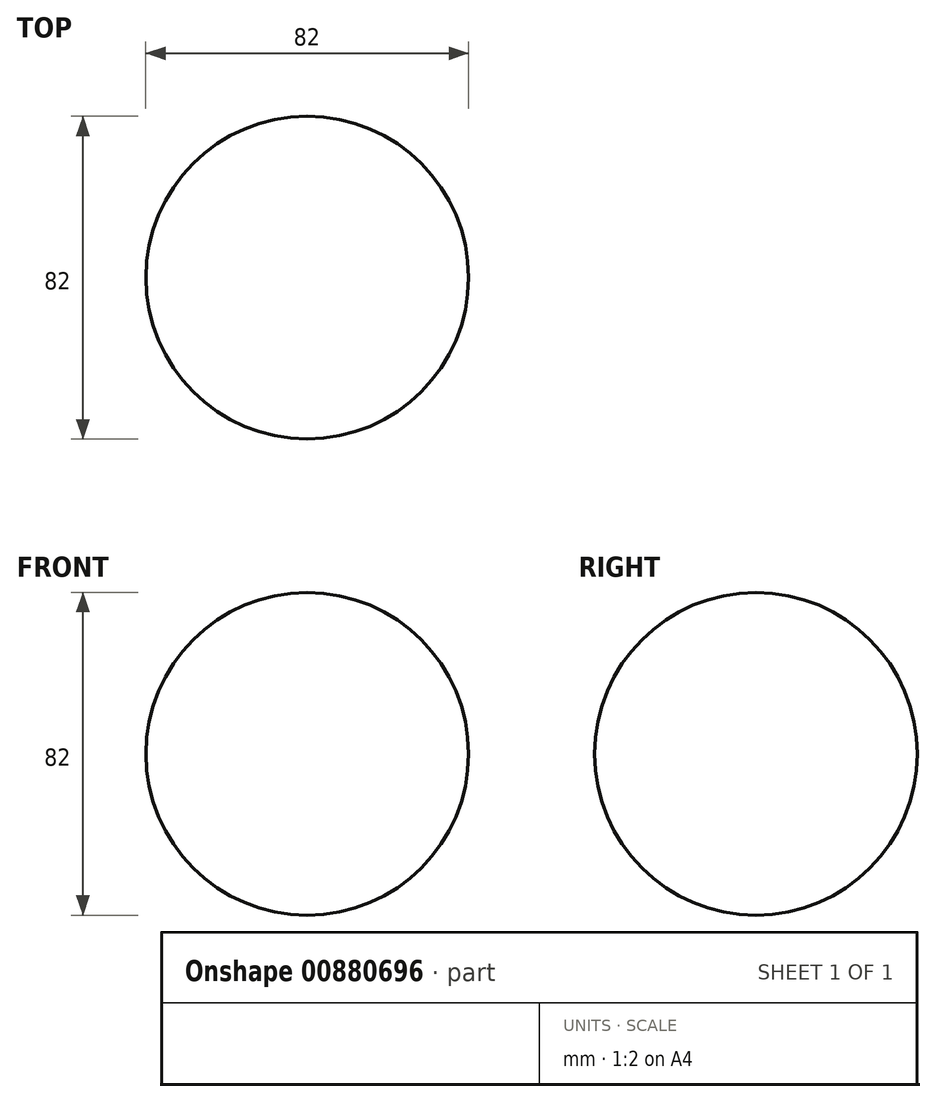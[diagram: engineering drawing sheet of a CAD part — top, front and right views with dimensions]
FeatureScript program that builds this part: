
annotation { "Feature Type Name" : "Feature", "Feature Type Description" : "" }
export const myFeature = defineFeature(function(context is Context, id is Id, definition is map)
    precondition{}
    {
        {
            var Q0;
            Q0=qCreatedBy(makeId("Front.planeOp"),FACE);
            var sketch = newSketch(context, id + "F0", { "sketchPlane" : qUnion([Q0])});
            skArc(sketch, "E0", {"start": v(0, -41) * mm, "mid": v(41, 0) * mm, "end": v(0, 41) * mm});
            skSolve(sketch);
        }
        {
            var Q0;
            Q0=qCreatedBy(makeId("Front.planeOp"),FACE);
            var sketch = newSketch(context, id + "F1", { "sketchPlane" : qUnion([Q0])});
            skLineSegment(sketch, "E1", {"start": v(0, 0) * mm, "end": v(0, 37.48) * mm, "construction": true});
            skSolve(sketch);
        }
        {
            var Q0;
            Q0=sQuery(id+"F0.wireOp",EDGE,"E0");
            var Q1;
            Q1=sQuery(id+"F1.wireOp",EDGE,"E1");
            revolve(context, id + "F2", {"bodyType" : ToolBodyType.SURFACE, "surfaceOperationType" : NewSurfaceOperationType.NEW, "surfaceEntities" : qUnion([Q0]), "axis" : qUnion([Q1]), "revolveType" : RevolveType.FULL});
        }
    });
